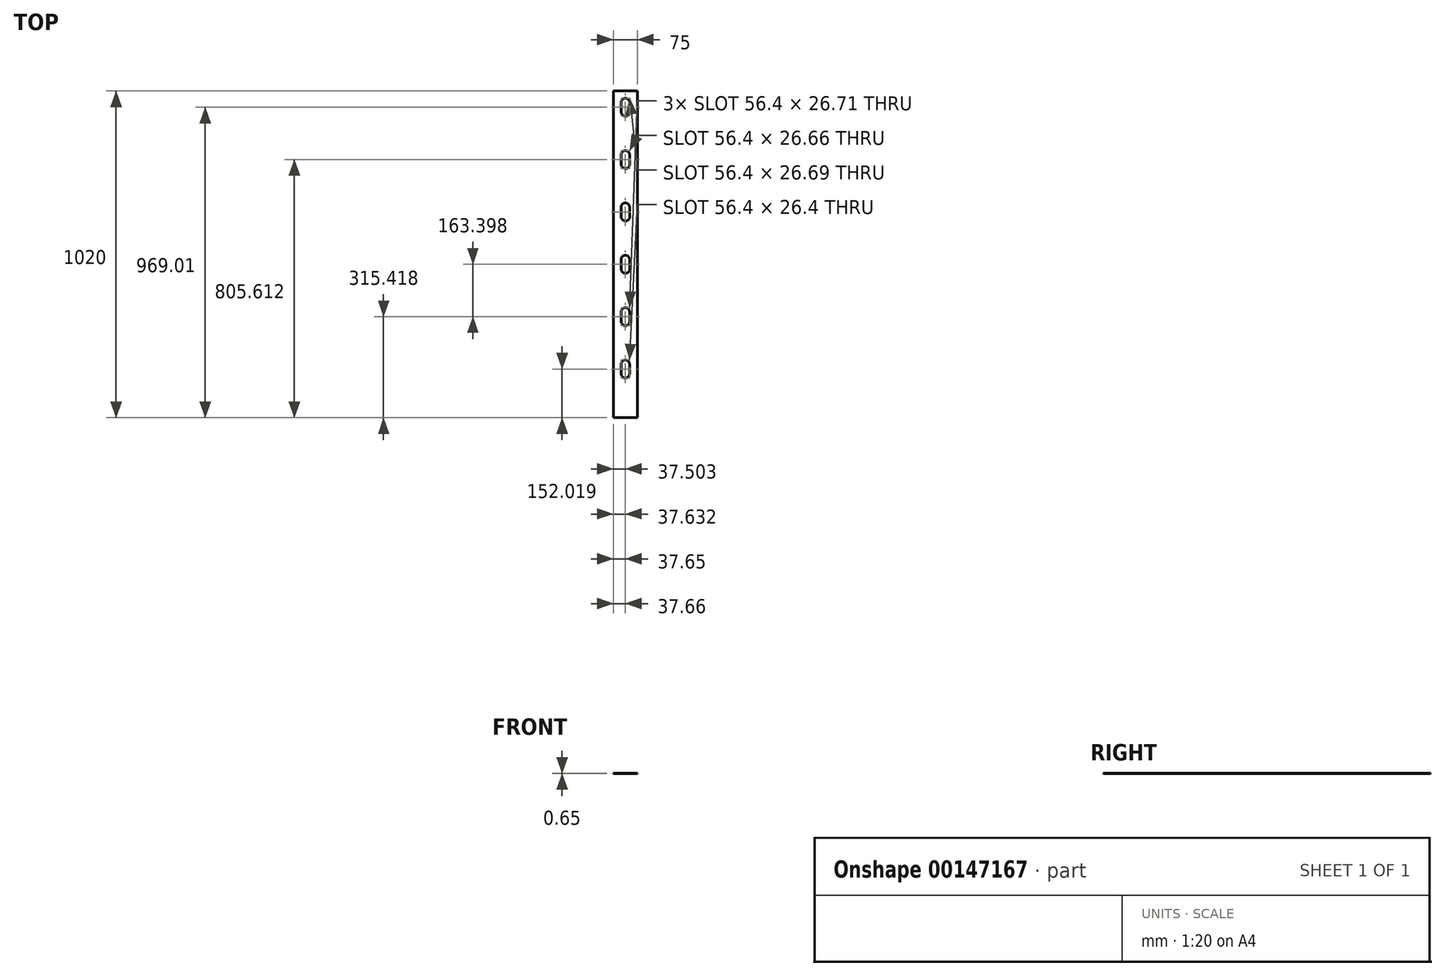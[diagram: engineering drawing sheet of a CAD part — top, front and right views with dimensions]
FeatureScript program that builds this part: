
annotation { "Feature Type Name" : "Feature", "Feature Type Description" : "" }
export const myFeature = defineFeature(function(context is Context, id is Id, definition is map)
    precondition{}
    {
        {
            var Q0;
            Q0=qCreatedBy(makeId("Top.planeOp"),FACE);
            var sketch = newSketch(context, id + "F0", { "sketchPlane" : qUnion([Q0])});
            skLineSegment(sketch, "E0.bottom", {"start": v(-88.8, -569.7) * mm, "end": v(-163.8, -569.7) * mm});
            skLineSegment(sketch, "E0.top", {"start": v(-88.8, 450.3) * mm, "end": v(-163.8, 450.3) * mm});
            skLineSegment(sketch, "E0.left", {"start": v(-88.8, -569.7) * mm, "end": v(-88.8, 450.3) * mm});
            skLineSegment(sketch, "E0.right", {"start": v(-163.8, -569.7) * mm, "end": v(-163.8, 450.3) * mm});
            skPoint(sketch, "E1.middle", {"position": v(148.88, -338.15) * mm});
            skArc(sketch, "E2", {"start": v(-139.5, -432.67) * mm, "mid": v(-126.3, -445.87) * mm, "end": v(-113.1, -432.67) * mm});
            skArc(sketch, "E3.trimOffspring", {"start": v(-113.1, -402.67) * mm, "mid": v(-126.3, -389.47) * mm, "end": v(-139.5, -402.67) * mm});
            skLineSegment(sketch, "E4", {"start": v(-139.5, -402.67) * mm, "end": v(-139.5, -432.67) * mm});
            skLineSegment(sketch, "E5", {"start": v(-113.1, -402.67) * mm, "end": v(-113.1, -432.67) * mm});
            skLineSegment(sketch, "E6", {"start": v(-126.3, -569.7) * mm, "end": v(-126.3, 450.3) * mm, "construction": true});
            skPoint(sketch, "E7.middle", {"position": v(216.86, -20.65) * mm});
            skPoint(sketch, "E8.middle", {"position": v(174.18, -74.29) * mm});
            skArc(sketch, "E9", {"start": v(-113.1, -239.13) * mm, "mid": v(-126.45, -226.07) * mm, "end": v(-139.5, -239.41) * mm});
            skArc(sketch, "E10", {"start": v(-139.2, -269.4) * mm, "mid": v(-125.85, -282.47) * mm, "end": v(-112.8, -269.13) * mm});
            skLineSegment(sketch, "E11", {"start": v(-113.1, -239.13) * mm, "end": v(-112.8, -269.13) * mm});
            skLineSegment(sketch, "E12", {"start": v(-139.5, -239.41) * mm, "end": v(-139.2, -269.4) * mm});
            skArc(sketch, "E13", {"start": v(-113.1, -75.74) * mm, "mid": v(-126.45, -62.68) * mm, "end": v(-139.5, -76.01) * mm});
            skArc(sketch, "E14", {"start": v(-139.2, -106.01) * mm, "mid": v(-125.85, -119.07) * mm, "end": v(-112.8, -105.73) * mm});
            skLineSegment(sketch, "E15", {"start": v(-113.1, -75.74) * mm, "end": v(-112.8, -105.73) * mm});
            skLineSegment(sketch, "E16", {"start": v(-139.5, -76.01) * mm, "end": v(-139.2, -106.01) * mm});
            skArc(sketch, "E17", {"start": v(-113.1, 87.66) * mm, "mid": v(-126.45, 100.72) * mm, "end": v(-139.5, 87.38) * mm});
            skArc(sketch, "E18", {"start": v(-139.19, 57.39) * mm, "mid": v(-125.85, 44.33) * mm, "end": v(-112.8, 57.66) * mm});
            skLineSegment(sketch, "E19", {"start": v(-113.1, 87.66) * mm, "end": v(-112.8, 57.66) * mm});
            skLineSegment(sketch, "E20", {"start": v(-139.5, 87.38) * mm, "end": v(-139.19, 57.39) * mm});
            skArc(sketch, "E21", {"start": v(-113.1, 251.03) * mm, "mid": v(-126.42, 264.12) * mm, "end": v(-139.5, 250.8) * mm});
            skArc(sketch, "E22", {"start": v(-139.25, 220.8) * mm, "mid": v(-125.94, 207.72) * mm, "end": v(-112.85, 221.04) * mm});
            skLineSegment(sketch, "E23", {"start": v(-113.1, 251.03) * mm, "end": v(-112.85, 221.04) * mm});
            skLineSegment(sketch, "E24", {"start": v(-139.5, 250.8) * mm, "end": v(-139.25, 220.8) * mm});
            skArc(sketch, "E25", {"start": v(-113.1, 414.45) * mm, "mid": v(-126.44, 427.52) * mm, "end": v(-139.5, 414.2) * mm});
            skArc(sketch, "E26", {"start": v(-139.21, 384.2) * mm, "mid": v(-125.88, 371.12) * mm, "end": v(-112.81, 384.45) * mm});
            skLineSegment(sketch, "E27", {"start": v(-113.1, 414.45) * mm, "end": v(-112.81, 384.45) * mm});
            skLineSegment(sketch, "E28", {"start": v(-139.5, 414.2) * mm, "end": v(-139.21, 384.2) * mm});
            skSolve(sketch);
        }
        {
            var Q0;
            Q0=qSketchRegion(id+"F0",true);
            var Q1;
            Q1=makeQuery(id+"F0.imprint","IMPRINT",FACE,{"disambiguationData":[TD([[makeQuery(id+"F0.imprint","IMPRINT",EDGE,{"derivedFrom":sQuery(id+"F0.wireOp",EDGE,"E0.bottom")}),-1.0]])]});
            extrude(context, id + "F1", {"entities" : qUnion([Q0, Q1]), "depth" : 0.65 * mm});
        }
    });
